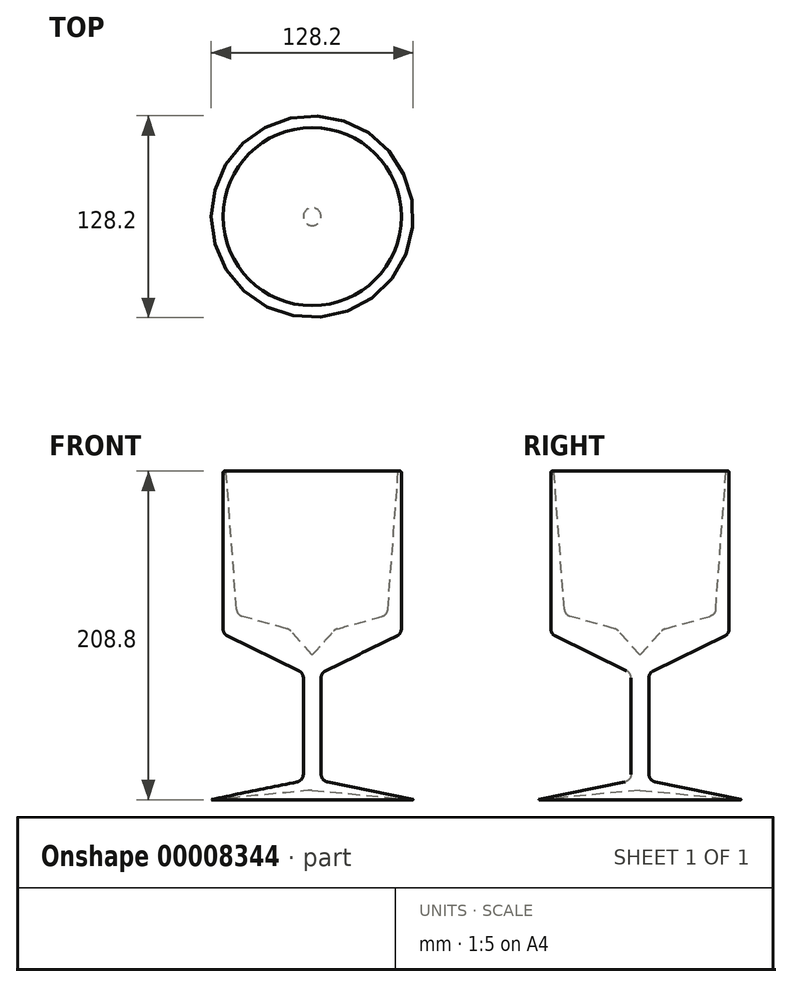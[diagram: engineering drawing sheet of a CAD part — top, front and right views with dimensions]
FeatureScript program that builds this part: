
annotation { "Feature Type Name" : "Feature", "Feature Type Description" : "" }
export const myFeature = defineFeature(function(context is Context, id is Id, definition is map)
    precondition{}
    {
        {
            var Q0;
            Q0=qCreatedBy(makeId("Front.planeOp"),FACE);
            var sketch = newSketch(context, id + "F0", { "sketchPlane" : qUnion([Q0])});
            skLineSegment(sketch, "E0", {"start": v(0, 6.29) * mm, "end": v(-65.85, 0) * mm});
            skLineSegment(sketch, "E1", {"start": v(-65.85, 0) * mm, "end": v(-5.65, 12.35) * mm});
            skLineSegment(sketch, "E2", {"start": v(-5.65, 12.35) * mm, "end": v(-5.65, 80.73) * mm});
            skLineSegment(sketch, "E3", {"start": v(-5.65, 80.73) * mm, "end": v(-56.6, 105.56) * mm});
            skLineSegment(sketch, "E4", {"start": v(-56.6, 105.56) * mm, "end": v(-56.6, 234.66) * mm});
            skLineSegment(sketch, "E5", {"start": v(-56.6, 234.66) * mm, "end": v(-47.8, 117.67) * mm});
            skLineSegment(sketch, "E6", {"start": v(-47.8, 117.67) * mm, "end": v(-14.55, 108.37) * mm});
            skLineSegment(sketch, "E7", {"start": v(-14.55, 108.37) * mm, "end": v(0, 92.06) * mm});
            skLineSegment(sketch, "E8", {"start": v(0, 92.06) * mm, "end": v(0, 6.29) * mm});
            skSolve(sketch);
        }
        {
            var Q0;
            Q0 = qSketchRegion(id + "F0", true);
            var Q1;
            Q1=sQuery(id+"F0.wireOp",EDGE,"E8");
            revolve(context, id + "F1", {"entities" : qUnion([Q0]), "axis" : qUnion([Q1]), "revolveType" : RevolveType.FULL});
        }
        {
            var Q0;
            Q0=makeQuery(id+"F1.opRevolve","SWEPT_EDGE",EDGE,{"disambiguationData":[OSD([sQuery(id+"F0.wireOp",EDGE,"E6"),sQuery(id+"F0.wireOp",EDGE,"E7")])]});
            fillet(context, id + "F2", {"entities" : qUnion([Q0]), "radius" : 5 * mm, "tangentPropagation" : true, "allowEdgeOverflow" : false});
        }
        {
            var Q0;
            Q0=makeQuery(id+"F1.opRevolve","SWEPT_EDGE",EDGE,{"disambiguationData":[OSD([sQuery(id+"F0.wireOp",EDGE,"E5"),sQuery(id+"F0.wireOp",EDGE,"E6")])]});
            fillet(context, id + "F3", {"entities" : qUnion([Q0]), "radius" : 5 * mm, "tangentPropagation" : true, "allowEdgeOverflow" : false});
        }
        {
            var Q0;
            Q0=makeQuery(id+"F1.opRevolve","SWEPT_EDGE",EDGE,{"disambiguationData":[OSD([sQuery(id+"F0.wireOp",EDGE,"E4"),sQuery(id+"F0.wireOp",EDGE,"E5")])]});
            fillet(context, id + "F4", {"entities" : qUnion([Q0]), "radius" : 1 * mm, "allowEdgeOverflow" : false});
        }
        {
            var Q0;
            Q0=makeQuery(id+"F1.opRevolve","SWEPT_EDGE",EDGE,{"disambiguationData":[OSD([sQuery(id+"F0.wireOp",EDGE,"E3"),sQuery(id+"F0.wireOp",EDGE,"E4")])]});
            fillet(context, id + "F5", {"entities" : qUnion([Q0]), "radius" : 5 * mm, "tangentPropagation" : true, "allowEdgeOverflow" : false});
        }
        {
            var Q0;
            Q0=makeQuery(id+"F1.opRevolve","SWEPT_EDGE",EDGE,{"disambiguationData":[OSD([sQuery(id+"F0.wireOp",EDGE,"E2"),sQuery(id+"F0.wireOp",EDGE,"E3")])]});
            fillet(context, id + "F6", {"entities" : qUnion([Q0]), "radius" : 5 * mm, "tangentPropagation" : true, "allowEdgeOverflow" : false});
        }
        {
            var Q0;
            Q0=makeQuery(id+"F1.opRevolve","SWEPT_EDGE",EDGE,{"disambiguationData":[OSD([sQuery(id+"F0.wireOp",EDGE,"E1"),sQuery(id+"F0.wireOp",EDGE,"E2")])]});
            fillet(context, id + "F7", {"entities" : qUnion([Q0]), "radius" : 5 * mm, "tangentPropagation" : true, "allowEdgeOverflow" : false});
        }
        {
            var Q0;
            Q0=makeQuery(id+"F1.opRevolve","SWEPT_EDGE",EDGE,{"disambiguationData":[OSD([sQuery(id+"F0.wireOp",EDGE,"E0"),sQuery(id+"F0.wireOp",EDGE,"E1")])]});
            fillet(context, id + "F8", {"entities" : qUnion([Q0]), "radius" : 0.1 * mm, "tangentPropagation" : true, "allowEdgeOverflow" : false});
        }
    });
